# Revit family: PD2 FP types Sans hôte
name_source: partatom
category: Dispositifs d'éclairage
units: mm (PartAtom-declared; Revit-internal decimal feet)

## family parameters
Basée sur le plan de construction = Oui
Conserver l'orientation des annotations = Non
Cote de connecteur circulaire = Utiliser le diamètre
Couper avec des vides une fois chargée = Non
Partagée = Non
Point de calcul de pièce = Non
Toujours verticalement = Oui
Type d'élément = Normal

## types (20) — shared parameters
Classe = II
Code d'assemblage = D5010200
Fabricant = B.E.G.
Hauteur de montage max = 300 cm
Image du type = 360°.jpg
Marque = LUXOMAT
Mode de pose = Faux Plafond
URL = http://www.luxomat.com
zero-valued in all types: Elévation par défaut

## per-type parameters (varying)
| type | Alimentation | Charge Cos ɸ =0.5 | Charge Cos ɸ =1 | Charge LED | Commentaires du type | Consommation | IP | Modèle | Relais | Référence | Température ambiante | Type de Sortie |
| 01- PD2 FP Générique | 110-240 V AC |  |  |  | DET.PRES.360°/Ø10M FAUX PLAFOND |  | 20 | PD2 FP |  |  | -25°C à +50°C |  |
| 02- PD2 M 1C FP réf 92565 | 110-240 V AC | 1150 VA | 2300 W | 300 W | DET.PRES.MAITRE.1 CONTACT.360°/Ø10M FAUX PLAFOND | 0,47 W | 20 | PD2 M 1C FP | 10 A | 92565 | -25°C à +50°C | TOR |
| 05- PD2N M DACO FP réf 93452 | 110-240 V AC | 0 | 0 | 0 | DET.PRES.MAITRE.DALI 2.360°/Ø10M FAUX PLAFOND | 2 W | 20 | PD2N M DACO FP | 0 | 93452 | -25°C à +50°C | DALI 2  (40 drivers maxi) |
| 17- PD2N LTMS FP réf 92113 | 11-48 V DC | 0 | 0 | 0 | DET.PRES.11-48V.1 CONTACT+ 2 SORTIES 0-10V (LUX/TEMPERATURE).360°/Ø10M FAUX PLAFOND | < 1 W | 20 | PD2N LTMS FP | 3 A | 92113 | -25°C à +50°C | TOR + 2 sorties 0-10 V (Lux/T°) |
| 08- PD2 S FP réf 92166 | 110-240 V AC | 0 | 0 | 0 | DET.PRES.ESCLAVE..360°/Ø10M FAUX PLAFOND | 0,25 W | 20 | PD2 S FP | 0 | 92166 | -25°C à +50°C | Esclave |
| 04- PD2 M 2C FP réf 92165 | 110-240 V AC | 1150 VA | 2300 W | 300 W | DET.PRES.MAITRE.2 CONTACTS.360°/Ø10M FAUX PLAFOND | 0,52 W | 20 | PD2 M 2C FP | 10 A / 3 A | 92165 | -25°C à +50°C | TOR + CVC |
| 06- PD2N M DACO 1C-FP réf 93455 | 110-240 V AC | 1150 VA | 2300 W | 300 W | DDET.PRES.MAITRE.DALI 2 + CONTACT NO.360°/Ø10M FAUX PLAFOND | 2 W | 20 | PD2N M DACO 1C FP | 10 A | 93455 | -25°C à +50°C | DALI 2 (40 drivers maxi) + Contact NO |
| 07- PD2 M DIM FP réf 92167 | 110-240 V AC | 1150 VA | 2300 W | 300 W | DET.PRES.MAITRE.DIM(1-10V).360°/Ø10M FAUX PLAFOND | 0,47 W | 23 | PD2 M DIM FP | 10 A | 92167 | -25°C à +50°C | DIM (50 ballasts maxi) |
| 19- PD2 M 2C 11-48V RR FP réf 92306 | 11-48 V AC/DC | 0 | 0 | 0 | DET.PRES.MAITRE.11-48V.2 CONTACTS.RR.360°/Ø10M FAUX PLAFOND | 0,76 W | 20 | PD2 M 2C 11-48V RR FP | 100 mA | 92306 | -25°C à +50°C | Reed Relais |
| 20- PD2 M 2C 11-48V 3A FP réf 92164 | 11-48 V AC/DC | 0 | 0 | 0 | DET.PRES.MAITRE.11-48V.2 CONTACTS.3A.360°/Ø10M FAUX PLAFOND | 0,95 W | 20 | PD2 M 2C 11-48V 3A FP | 3 A | 92164 | -25°C à +50°C | Reed Relais |
| 16- PD2N LON FP réf 92736 | 24 V DC par Bus LON | 0 | 0 | 0 | DET.PRES.LON.360°/Ø10M FAUX PLAFOND | 12 mA | 20 | PD2N LON FP | 0 | 92736 | +5°C à +50°C | LON |
| 15- PD2N KNXs DX FP réf 93512 | 24 V DC par Bus KNX | 0 | 0 | 0 | DET.PRES.KNX Sécure.VERSION DELUXE.360°/Ø10M FAUX PLAFOND | 12 mA | 20 | PD2N KNXs DX FP | 0 | 93512 | -5°C à +45°C | KNX Sécure - 1 sortie Eclairage TOR ou GRADATION / 3 sorties Présence / Capteur de température et bruit / HCL |
| 03- PD2N LED M 1C FP réf 94055 | 110-240 V AC | 1150 VA | 2300 W | 300 W | DET.PRES.MAITRE.1 CONTACT + BALISAGE.360°/Ø10M FAUX PLAFOND | 0,47 W | 20 | PD2N LED M 1C FP | 10 A | 94055 | -25°C à +50°C | TOR + Balisage LED intégré |
| 18- PD2N LTMS RR FP réf 92119 | 11-48 V DC | 0 | 0 | 0 | DET.PRES.11-48V.1 CONTACT.RR.360°/Ø10M FAUX PLAFOND | >0,5 W | 20 | PD2N LTMS RR FP | 100 mA | 92119 | -25°C à +50°C | Reed Relais |
| 11- PD2N KNX BA FP réf 93380 | 24 V DC par Bus KNX | 0 | 0 | 0 | DET.PRES.KNX.VERSION BASIQUE.360°/Ø10M FAUX PLAFOND | 12 mA | 20 | PD2N KNX BA FP | 0 | 93380 | -5°C à +45°C | KNX - 1 sortie Eclairage TOR |
| 12- PD2N KNX ST FP réf 93382 | 24 V DC par Bus KNX | 0 | 0 | 0 | DET.PRES.KNX.VERSION STANDARD.360°/Ø10M FAUX PLAFOND | 12 mA | 20 | PD2N KNX ST FP | 0 | 93382 | -5°C à +45°C | KNX - 1 sortie Eclairage TOR ou GRADATION / 3 sorties Présence |
| 09- PD2N DALISYS FP réf 93369 | 24 V DC par Bus KNX | 0 | 0 | 0 | MULTI.CAPTEUR.PRES.DALISYS.360°/Ø10M FAUX PLAFOND | 3 mA | 20 | PD2N DALISYS FP | 0 | 93369 | -25°C à +55°C | DALI Adressable |
| 10- PD2N BMS DALI 2 FP réf 93543 | 24 V DC par Bus KNX | 0 | 0 | 0 | MULTI.CAPTEUR.PRES.BMS.DALI 2.360°/Ø10M FAUX PLAFOND | 7 mA | 20 | PD2N BMS DALI 2 FP | 0 | 93543 | -25°C à +55°C | DALI 2 Adressable - BMS |
| 14- PD2N KNXs ST FP réf 93510 | 24 V DC par Bus KNX | 0 | 0 | 0 | DET.PRES.KNX Sécure.VERSION STANDARD.360°/Ø10M FAUX PLAFOND | 12 mA | 20 | PD2N KNXs ST FP | 0 | 93510 | -5°C à +45°C | KNX Sécure - 1 sortie Eclairage TOR ou GRADATION / 3 sorties Présence / HCL |
| 13- PD2N KNX DX FP réf 93360 | 24 V DC par Bus KNX | 0 | 0 | 0 | DET.PRES.KNX.VERSION DELUXE.360°/Ø10M FAUX PLAFOND | 12 mA | 20 | PD2N KNX DX FP | 0 | 93360 | -5°C à +45°C | KNX - 1 sortie Eclairage TOR ou GRADATION / 3 sorties Présence / Capteur de température et bruit |
